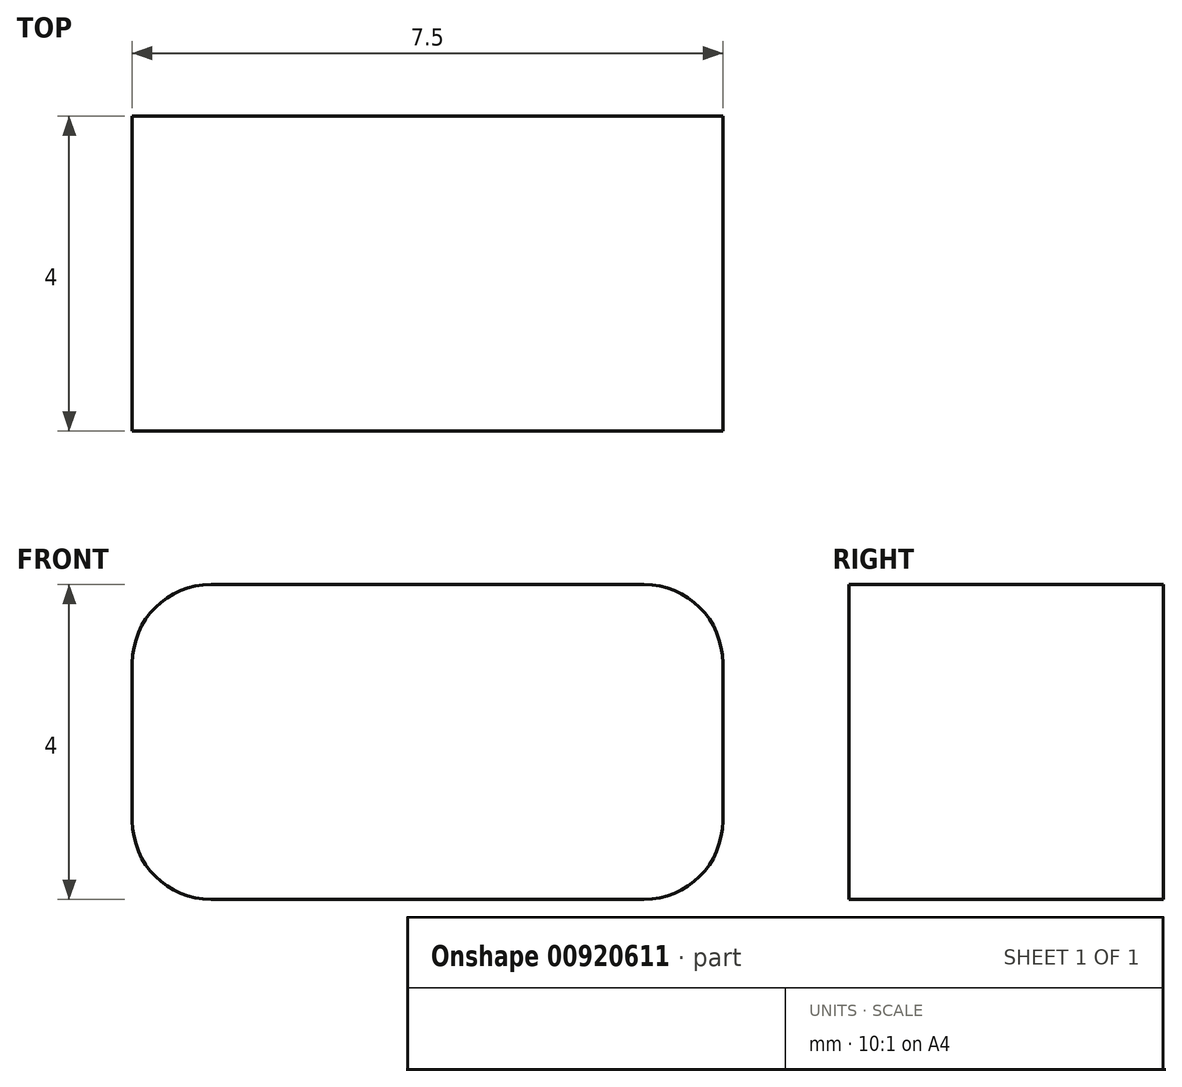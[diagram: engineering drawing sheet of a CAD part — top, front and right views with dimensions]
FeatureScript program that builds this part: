
annotation { "Feature Type Name" : "Feature", "Feature Type Description" : "" }
export const myFeature = defineFeature(function(context is Context, id is Id, definition is map)
    precondition{}
    {
        {
            var Q0;
            Q0=qCreatedBy(makeId("Front.planeOp"),FACE);
            var sketch = newSketch(context, id + "F0", { "sketchPlane" : qUnion([Q0])});
            skLineSegment(sketch, "E0.bottom", {"start": v(3.75, 2) * mm, "end": v(-3.75, 2) * mm});
            skLineSegment(sketch, "E0.top", {"start": v(3.75, -2) * mm, "end": v(-3.75, -2) * mm});
            skLineSegment(sketch, "E0.left", {"start": v(3.75, 2) * mm, "end": v(3.75, -2) * mm});
            skLineSegment(sketch, "E0.right", {"start": v(-3.75, 2) * mm, "end": v(-3.75, -2) * mm});
            skPoint(sketch, "E0.middle", {"position": v(0, 0) * mm});
            skSolve(sketch);
        }
        {
            var Q0;
            Q0=makeQuery(id+"F0.imprint","IMPRINT",FACE,{"disambiguationData":[TD([[makeQuery(id+"F0.imprint","IMPRINT",EDGE,{"derivedFrom":sQuery(id+"F0.wireOp",EDGE,"E0.bottom")}),1.0]])]});
            extrude(context, id + "F1", {"entities" : qUnion([Q0]), "depth" : 4 * mm, "offsetDistance" : 25 * mm, "symmetric" : true});
        }
        {
            var Q0;
            Q0=makeQuery(id+"F1.opExtrude","SWEPT_EDGE",EDGE,{"disambiguationData":[OSD([sQuery(id+"F0.wireOp",EDGE,"E0.bottom"),sQuery(id+"F0.wireOp",EDGE,"E0.right")])]});
            var Q1;
            Q1=makeQuery(id+"F1.opExtrude","SWEPT_EDGE",EDGE,{"disambiguationData":[OSD([sQuery(id+"F0.wireOp",EDGE,"E0.top"),sQuery(id+"F0.wireOp",EDGE,"E0.right")])]});
            var Q2;
            Q2=makeQuery(id+"F1.opExtrude","SWEPT_EDGE",EDGE,{"disambiguationData":[OSD([sQuery(id+"F0.wireOp",EDGE,"E0.bottom"),sQuery(id+"F0.wireOp",EDGE,"E0.left")])]});
            var Q3;
            Q3=makeQuery(id+"F1.opExtrude","SWEPT_EDGE",EDGE,{"disambiguationData":[OSD([sQuery(id+"F0.wireOp",EDGE,"E0.top"),sQuery(id+"F0.wireOp",EDGE,"E0.left")])]});
            fillet(context, id + "F2", {"entities" : qUnion([Q0, Q1, Q2, Q3]), "radius" : 1 * mm, "tangentPropagation" : true, "allowEdgeOverflow" : false});
        }
    });
